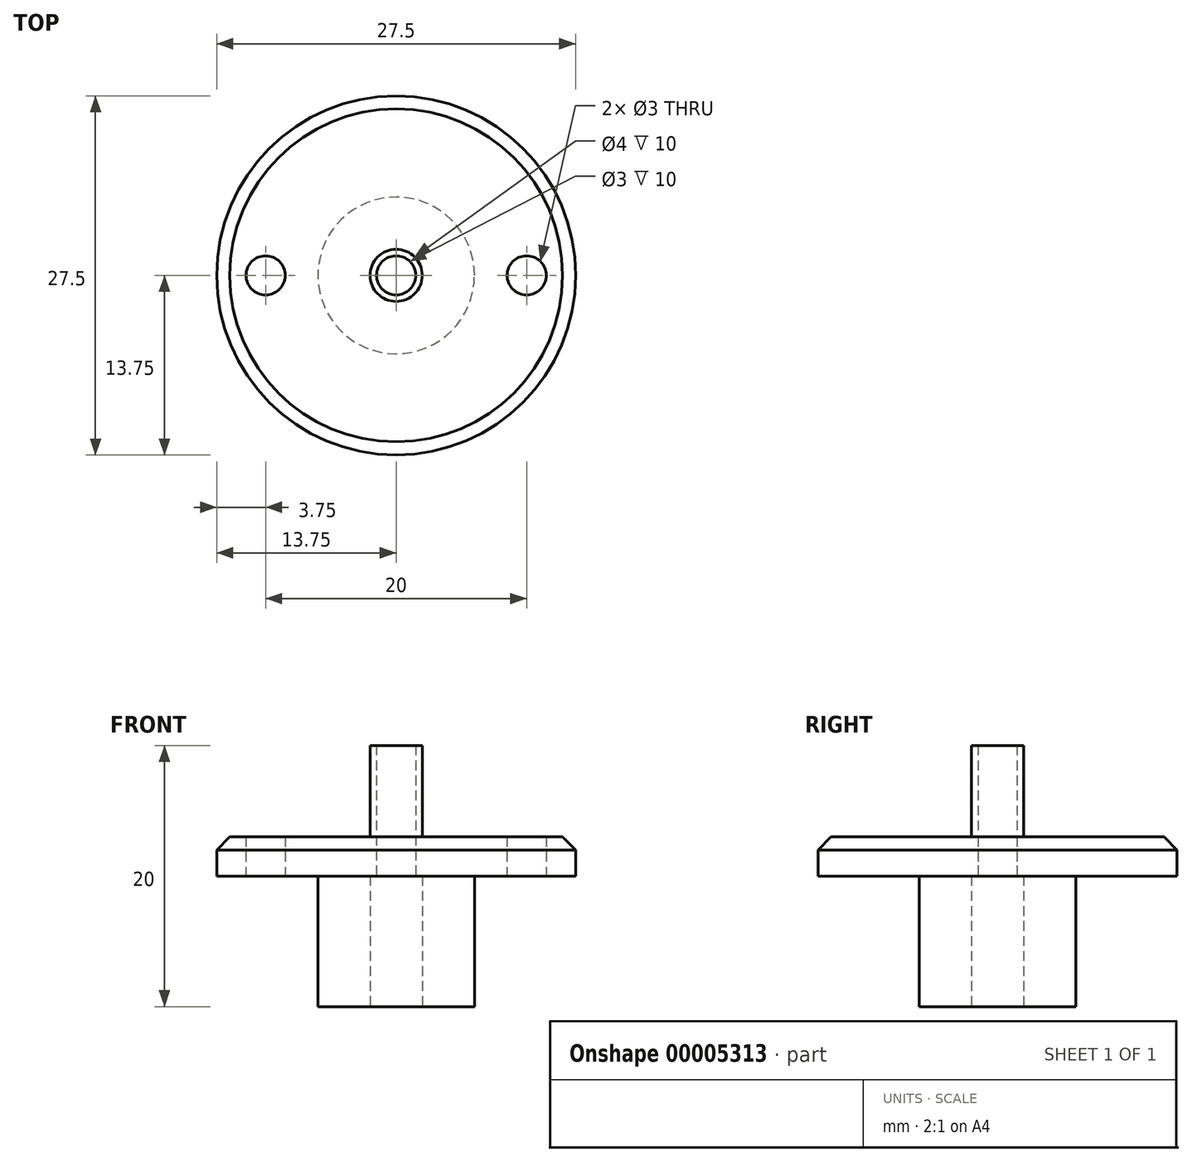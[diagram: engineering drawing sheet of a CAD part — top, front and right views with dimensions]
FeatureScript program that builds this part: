
annotation { "Feature Type Name" : "Feature", "Feature Type Description" : "" }
export const myFeature = defineFeature(function(context is Context, id is Id, definition is map)
    precondition{}
    {
        {
            var Q0;
            Q0=qCreatedBy(makeId("Top.planeOp"),FACE);
            var sketch = newSketch(context, id + "F0", { "sketchPlane" : qUnion([Q0])});
            skCircle(sketch, "E0", {"center": v(0, 0) * mm, "radius": 2 * mm});
            skCircle(sketch, "E1", {"center": v(0, 0) * mm, "radius": 6 * mm});
            skCircle(sketch, "E2", {"center": v(0, 0) * mm, "radius": 13.75 * mm});
            skCircle(sketch, "E3", {"center": v(-10, 0) * mm, "radius": 1.5 * mm});
            skCircle(sketch, "E4", {"center": v(10, 0) * mm, "radius": 1.5 * mm});
            skCircle(sketch, "E5", {"center": v(0, 0) * mm, "radius": 1.5 * mm});
            skSolve(sketch);
        }
        {
            var Q0;
            Q0=makeQuery(id+"F0.imprint","IMPRINT",FACE,{"disambiguationData":[TD([[makeQuery(id+"F0.imprint","IMPRINT",EDGE,{"derivedFrom":sQuery(id+"F0.wireOp",EDGE,"E0")}),-1.0]])]});
            var Q1;
            Q1=makeQuery(id+"F0.imprint","IMPRINT",FACE,{"disambiguationData":[TD([[makeQuery(id+"F0.imprint","IMPRINT",EDGE,{"derivedFrom":sQuery(id+"F0.wireOp",EDGE,"E1")}),-1.0]])]});
            extrude(context, id + "F1", {"entities" : qUnion([Q0, Q1]), "depth" : 3 * mm});
        }
        {
            var Q0;
            Q0=makeQuery(id+"F0.imprint","IMPRINT",FACE,{"disambiguationData":[TD([[makeQuery(id+"F0.imprint","IMPRINT",EDGE,{"derivedFrom":sQuery(id+"F0.wireOp",EDGE,"E0")}),-1.0]])]});
            extrude(context, id + "F2", {"entities" : qUnion([Q0]), "operationType" : NewBodyOperationType.ADD, "oppositeDirection" : true, "depth" : 10 * mm});
        }
        {
            var Q0;
            Q0=makeQuery(id+"F1.opExtrude","CAP_EDGE",EDGE,{"disambiguationData":[OSD([sQuery(id+"F0.wireOp",EDGE,"E2")])],"isStart":false});
            chamfer(context, id + "F3", {"entities" : qUnion([Q0]), "chamferType" : ChamferType.TWO_OFFSETS, "width1" : 1 * mm, "oppositeDirection" : false, "width2" : 1 * mm, "tangentPropagation" : true});
        }
        {
            var Q0;
            Q0=makeQuery(id+"F0.imprint","IMPRINT",FACE,{"disambiguationData":[TD([[makeQuery(id+"F0.imprint","IMPRINT",EDGE,{"derivedFrom":sQuery(id+"F0.wireOp",EDGE,"E0")}),1.0]])]});
            extrude(context, id + "F4", {"entities" : qUnion([Q0]), "operationType" : NewBodyOperationType.ADD, "depth" : 10 * mm});
        }
    });
